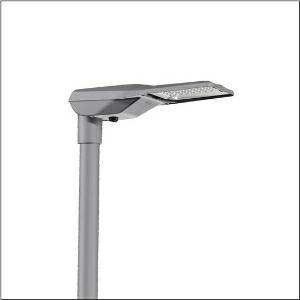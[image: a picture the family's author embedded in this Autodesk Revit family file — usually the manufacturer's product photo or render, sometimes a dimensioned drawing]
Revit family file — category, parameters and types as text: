
# Revit family: streetlight_sl_21_mini___st1_0ab_5xe2m33r08jb_ae43
name_source: partatom
category: Lighting Fixtures
units: mm (PartAtom-declared; Revit-internal decimal feet)

## family parameters
Cut with Voids When Loaded = No
Host = Face
Light Source = No
Part Type = Normal
Room Calculation Point = No
Round Connector Dimension = Use Diameter
Shared = No

## types (1)
- --- (1 x LED, 11390 lm, 88.6 W, 3000K)
    Apparent Load = 89 VA
    CIE Flux Codes = 40 74 97 100 100
    Color Rendering = 70
    Color Temperature = 3000K
    Default Elevation = 1800 mm
    Description = Streetlight SL 21 mini, mast luminaire, primary light control with lens, of PMMA, primary optical cover: cover, of toughened safety glass, transparent, light distribution: ST1.0aB, light emission: direct distribution, primary light characteristic: asymmetric, installation type: side-entry, post-top, LED, High Power LED, rated luminous flux: 11.390lm, luminous efficacy: 129lm/W, light colour: 730, colour temperature: 3000K, control gear: D4i, control: flexible luminous flux parameterisation, time-dependent luminous flux control, constant luminous flux control, overheat protection, pre-setting: logarithmic dimming characteristic, mains connection: 220..240V, AC, 50/60Hz, start of lifetime: 89W, end of service life: 92W, reduction: 41W, luminaire housing, of diecast aluminium, powder-coated, Siteco® metallic grey (DB 702S), corrosivity category C5 mid according to DIN EN ISO 12944, please order mast flange separately, inclination adjustable: 0°, 5°, 10°, 15°, sealing non-destructively replaceable, multi-level sealing system, length: 628mm, width: 235mm, height: 110mm, mast flange for spigot size: 42mm (side-entry): 5XC10008XM4, 60/48mm (side-entry/post-top): 5XC10108XM2, 76/60mm (side-entry/post-top): 5XC10108XM1, mounting height: 4..8m, Smart Interface below, protection rating (complete): IP66, insulation class (complete): insulation class II (safety insulation), certification: CE, ENEC, ENEC+, VDE, impact resistance: IK10, permissible operating ambient temperature for outdoor applications: -40..+50°C, standard-compliant lighting for roads and squares, packaging unit: 1 piece

Light Distribution: ST1.0aB
    Height = 110 mm
    Lamp = 1 x LED
    Lamp Light Flux = 11390 lm
    Lamp Power = 88.6 W
    Lamp count = 1
    Length = 625 mm
    Luminous efficacy = 129 lm/W
    Manufacturer = Siteco
    ModVariant = No
    Model = 5XE2M33R08JB
    Number of Poles = 1
    OnlyDefault = Yes
    Power Factor = 1
    Product Name = Streetlight SL 21 mini | ST1.0aB
    Product group = mast luminaire | pylon top
    ProductGroupID = 6100
    Protection Class = Protection class II
    Protection Degree = IP 66
    RLX_Detail_Level = 1
    RLX_Emergency_Light_Flux = 0 lm
    RLX_Emergency_Type = 0
    RLX_Emergency_Type_DB = No
    RlxData = <blob elided: 26329 chars, md5=828bfea0>
    Socket = socket
    Standby Power = 0 W
    System Light Flux = 11390 lm
    System Power = 89 W
    Type Comments = factory setting: luminous flux: 100 % | dim-lin: 254 | 915 mA
    Type Image = l_1003516.jpg
    URL = http://relux.com
    VarID = @adj_030793
    Voltage = 0 V
    Weight = 0.00 kg
    Width = 234 mm

## geometry (parser evidence)
native form markers: Blend x4, Sweep x11
no freeform markers — native parametric forms only
